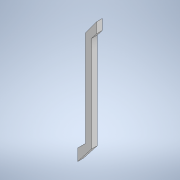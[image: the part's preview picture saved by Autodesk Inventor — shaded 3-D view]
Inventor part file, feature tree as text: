
AUTODESK INVENTOR PART (.ipt)
format: ipt  version: 2021 (Build 250183000, 183)  size: 108,032 bytes
history: native  units: mm
features: extrude x1, sketch x1
ambient origin geometry x8: Origin, YZ Plane, XZ Plane, XY Plane, X Axis, Y Axis, Z Axis, Center Point
bodies: Solide1 (feature_tree)
feature tree (2):
  extrude  "Extrusion1"  Depth=147.0mm
  sketch  "Esquisse1"
